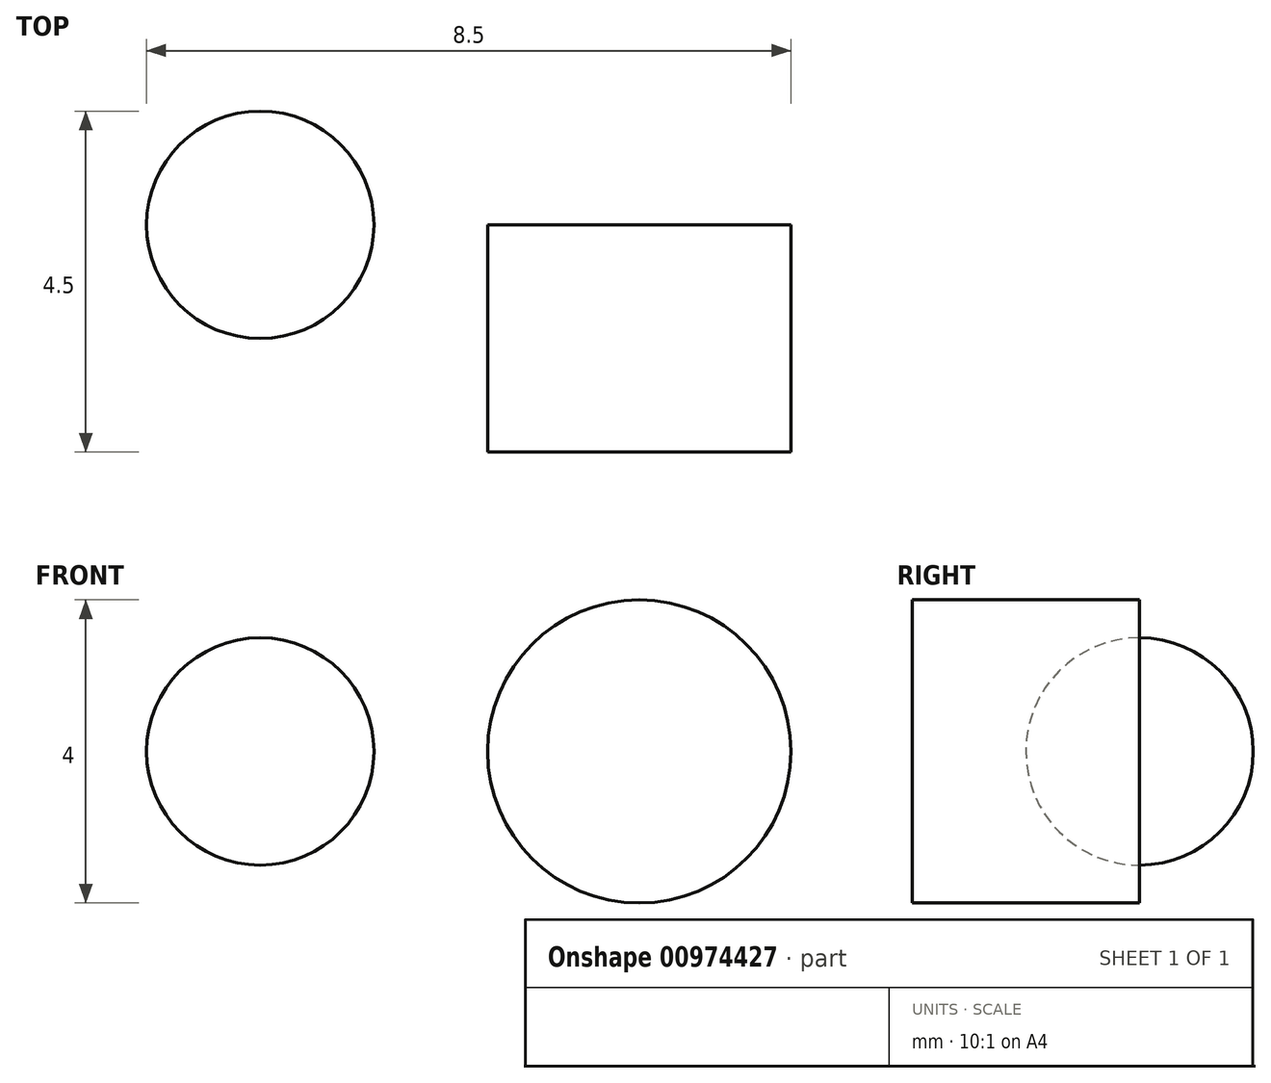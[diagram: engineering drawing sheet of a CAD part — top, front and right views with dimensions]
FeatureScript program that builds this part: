
annotation { "Feature Type Name" : "Feature", "Feature Type Description" : "" }
export const myFeature = defineFeature(function(context is Context, id is Id, definition is map)
    precondition{}
    {
        {
            var Q0;
            Q0=qCreatedBy(makeId("Top.planeOp"),FACE);
            var sketch = newSketch(context, id + "F0", { "sketchPlane" : qUnion([Q0])});
            skCircle(sketch, "E0", {"center": v(0, 0) * mm, "radius": 2.5 * mm});
            skLineSegment(sketch, "E1.bottom", {"start": v(2, 1.5) * mm, "end": v(-2, 1.5) * mm});
            skLineSegment(sketch, "E1.top", {"start": v(2, -1.5) * mm, "end": v(-2, -1.5) * mm});
            skLineSegment(sketch, "E1.left", {"start": v(2, 1.5) * mm, "end": v(2, -1.5) * mm});
            skLineSegment(sketch, "E1.right", {"start": v(-2, 1.5) * mm, "end": v(-2, -1.5) * mm});
            skSolve(sketch);
        }
        {
            var Q0;
            Q0=qCreatedBy(makeId("Front.planeOp"),FACE);
            var sketch = newSketch(context, id + "F1", { "sketchPlane" : qUnion([Q0])});
            skCircle(sketch, "E2", {"center": v(0, 0) * mm, "radius": 2 * mm});
            skSolve(sketch);
        }
        {
            var Q0;
            Q0 = qSketchRegion(id + "F1", true);
            extrude(context, id + "F2", {"entities" : qUnion([Q0]), "depth" : 3 * mm, "offsetDistance" : 25 * mm});
        }
        {
            var Q0;
            Q0=qCreatedBy(makeId("Front.planeOp"),FACE);
            var sketch = newSketch(context, id + "F3", { "sketchPlane" : qUnion([Q0])});
            skArc(sketch, "E3", {"start": v(-5, -1.5) * mm, "mid": v(-3.5, 0) * mm, "end": v(-5, 1.5) * mm});
            skLineSegment(sketch, "E4", {"start": v(-5, 1.5) * mm, "end": v(-5, -1.5) * mm});
            skSolve(sketch);
        }
        {
            var Q0;
            Q0=makeQuery(id+"F3.imprint","IMPRINT",FACE,{"disambiguationData":[TD([[makeQuery(id+"F3.imprint","IMPRINT",EDGE,{"derivedFrom":sQuery(id+"F3.wireOp",EDGE,"E3")}),1.0]])]});
            var Q1;
            Q1=sQuery(id+"F3.wireOp",EDGE,"E4");
            revolve(context, id + "F4", {"surfaceOperationType" : NewSurfaceOperationType.NEW, "entities" : qUnion([Q0]), "axis" : qUnion([Q1]), "revolveType" : RevolveType.FULL});
        }
    });
